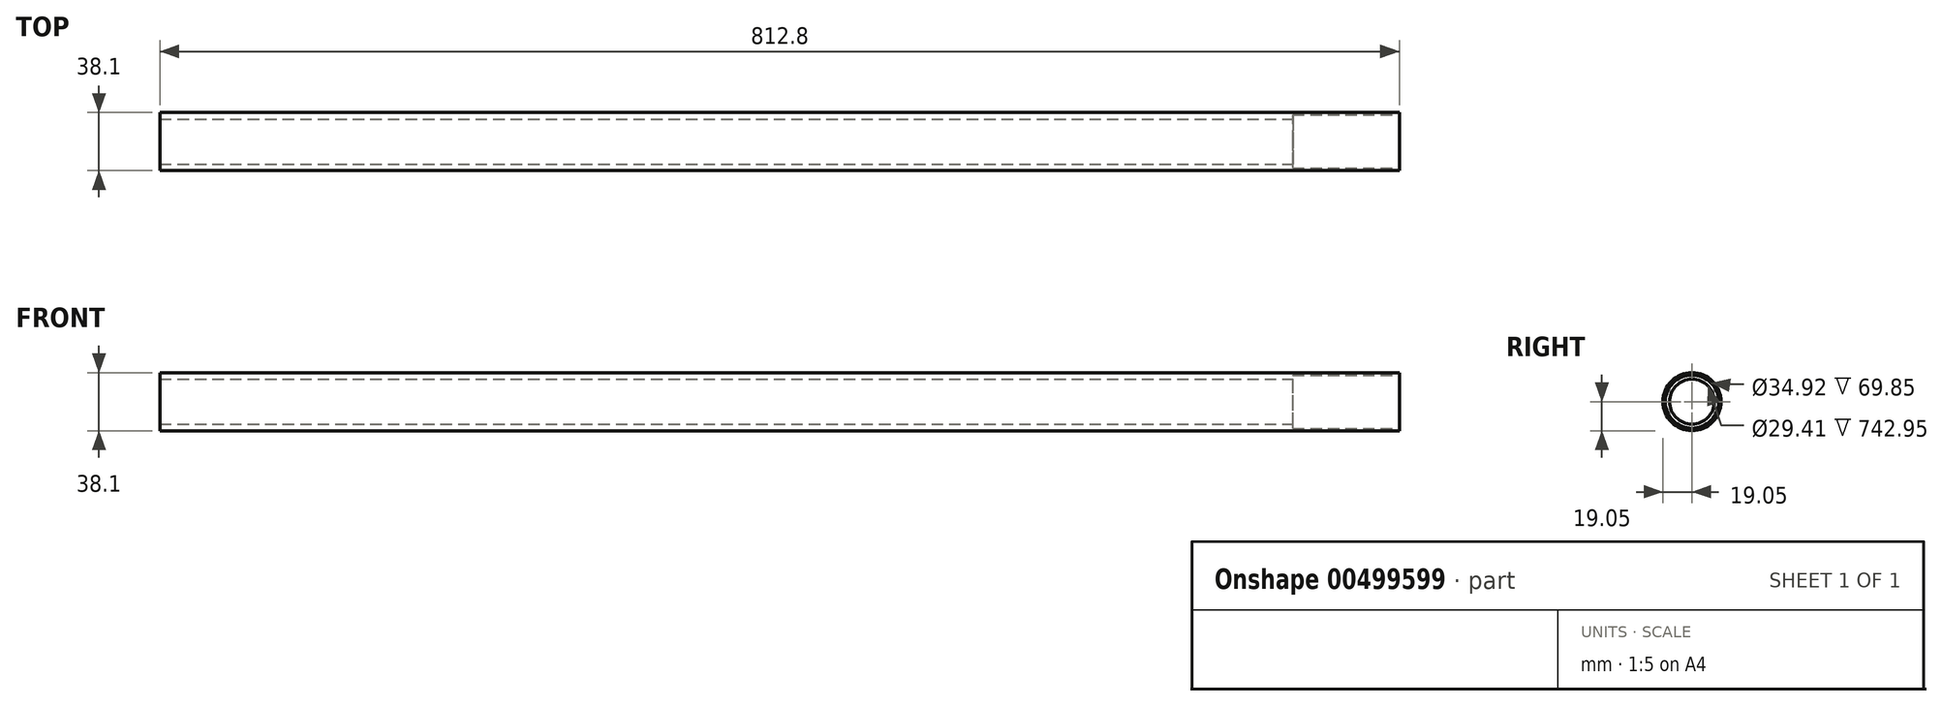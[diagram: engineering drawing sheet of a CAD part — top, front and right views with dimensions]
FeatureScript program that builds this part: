
annotation { "Feature Type Name" : "Feature", "Feature Type Description" : "" }
export const myFeature = defineFeature(function(context is Context, id is Id, definition is map)
    precondition{}
    {
        {
            var Q0;
            Q0=qCreatedBy(makeId("Right.planeOp"),FACE);
            var sketch = newSketch(context, id + "F0", { "sketchPlane" : qUnion([Q0])});
            skCircle(sketch, "E0", {"center": v(0, 0) * mm, "radius": 19.05 * mm});
            skSolve(sketch);
        }
        {
            var Q0;
            Q0=makeQuery(id+"F0.imprint","IMPRINT",FACE,{"disambiguationData":[TD([[makeQuery(id+"F0.imprint","IMPRINT",EDGE,{"derivedFrom":sQuery(id+"F0.wireOp",EDGE,"E0")}),1.0]])]});
            extrude(context, id + "F1", {"entities" : qUnion([Q0]), "depth" : 812.8 * mm, "offsetDistance" : 25.4 * mm});
        }
        {
            var Q0;
            Q0=makeQuery(id+"F1.opExtrude","CAP_FACE",FACE,{"disambiguationData":[OSD([sQuery(id+"F0.wireOp",EDGE,"E0")])],"isStart":false});
            var sketch = newSketch(context, id + "F2", { "sketchPlane" : qUnion([Q0])});
            skCircle(sketch, "E1", {"center": v(0, 0) * mm, "radius": 17.46 * mm});
            skSolve(sketch);
        }
        {
            var Q0;
            Q0 = qSketchRegion(id + "F2", true);
            extrude(context, id + "F3", {"entities" : qUnion([Q0]), "operationType" : NewBodyOperationType.REMOVE, "oppositeDirection" : true, "depth" : 69.85 * mm, "offsetDistance" : 25.4 * mm});
        }
        {
            var Q0;
            Q0=makeQuery(id+"F3.boolean.opBoolean","COPY",FACE,{"derivedFrom":makeQuery(id+"F3.opExtrude","CAP_FACE",FACE,{"disambiguationData":[OSD([sQuery(id+"F2.wireOp",EDGE,"E1")])],"isStart":false})});
            var sketch = newSketch(context, id + "F4", { "sketchPlane" : qUnion([Q0])});
            skCircle(sketch, "E2", {"center": v(0, 0) * mm, "radius": 14.7 * mm});
            skSolve(sketch);
        }
        {
            var Q0;
            Q0=makeQuery(id+"F4.imprint","IMPRINT",FACE,{"disambiguationData":[TD([[makeQuery(id+"F4.imprint","IMPRINT",EDGE,{"derivedFrom":sQuery(id+"F4.wireOp",EDGE,"E2")}),1.0]])]});
            extrude(context, id + "F5", {"entities" : qUnion([Q0]), "operationType" : NewBodyOperationType.REMOVE, "endBound" : BoundingType.THROUGH_ALL, "oppositeDirection" : true, "depth" : 25.4 * mm});
        }
    });
